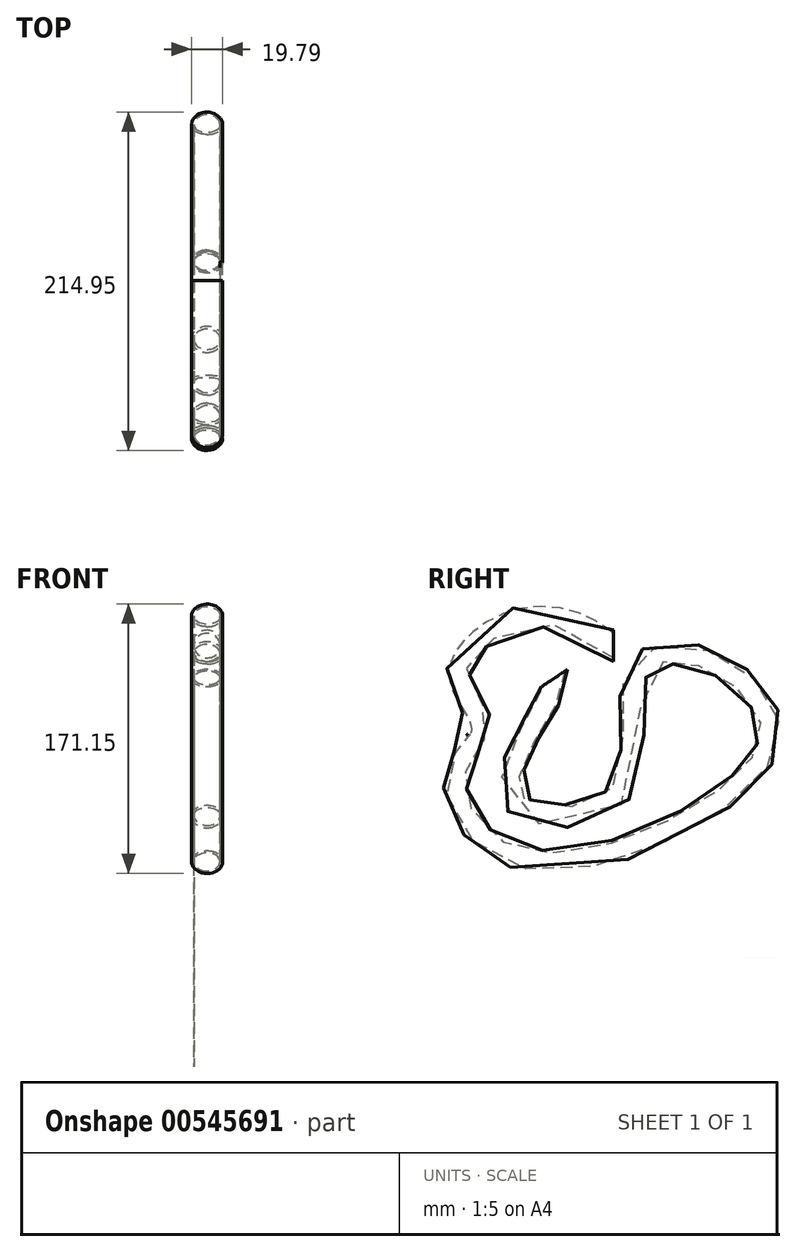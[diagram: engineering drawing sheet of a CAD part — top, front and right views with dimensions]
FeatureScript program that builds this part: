
annotation { "Feature Type Name" : "Feature", "Feature Type Description" : "" }
export const myFeature = defineFeature(function(context is Context, id is Id, definition is map)
    precondition{}
    {
        {
            var Q0;
            Q0=qCreatedBy(makeId("Front.planeOp"),FACE);
            var sketch = newSketch(context, id + "F0", { "sketchPlane" : qUnion([Q0])});
            skCircle(sketch, "E0", {"center": v(38.81, 52.04) * mm, "radius": 9.9 * mm});
            skSolve(sketch);
        }
        {
            var Q0;
            Q0=qCreatedBy(makeId("Right.planeOp"),FACE);
            var sketch = newSketch(context, id + "F1", { "sketchPlane" : qUnion([Q0])});
            skFitSpline(sketch, "E1", {"points": [v(0, 52.04) * mm, v(-97.44, 38.65) * mm, v(-86.04, 3) * mm, v(-99.74, -31.72) * mm, v(-63.33, -81.38) * mm, v(57.34, -52.76) * mm, v(99.12, 0) * mm, v(61.05, 42.37) * mm, v(15.06, 35.34) * mm, v(3.88, -40.66) * mm, v(-61, -47.6) * mm, v(-51.73, 0) * mm, v(-37.34, 31.54) * mm], "startDerivative": vector(-1188.57, 1102.25) * mm, "endDerivative": vector(104.06, 624.38) * mm});
            skSolve(sketch);
        }
        {
            var Q0;
            Q0 = qSketchRegion(id + "F0", true);
            var Q1;
            Q1 = qConstructionFilter(qBodyType(qCreatedBy(id + "F1" ,EDGE), BodyType.WIRE), ConstructionObject.NO);
            sweep(context, id + "F2", {"profiles" : qUnion([Q0]), "path" : qUnion([Q1])});
        }
        {
            var Q0;
            Q0=makeQuery(id+"F2.opSweep","CAP_FACE",FACE,{"disambiguationData":[OSD([sQuery(id+"F0.wireOp",EDGE,"E0"),sQuery(id+"F1.wireOp",VERTEX,"E1.start")])],"isStart":true});
            var Q1;
            Q1=makeQuery(id+"F2.opSweep","CAP_FACE",FACE,{"disambiguationData":[OSD([sQuery(id+"F0.wireOp",EDGE,"E0"),sQuery(id+"F1.wireOp",VERTEX,"E1.end")])],"isStart":false});
            shell(context, id + "F3", {"entities" : qUnion([Q0, Q1]), "thickness" : 1.5 * mm});
        }
    });
